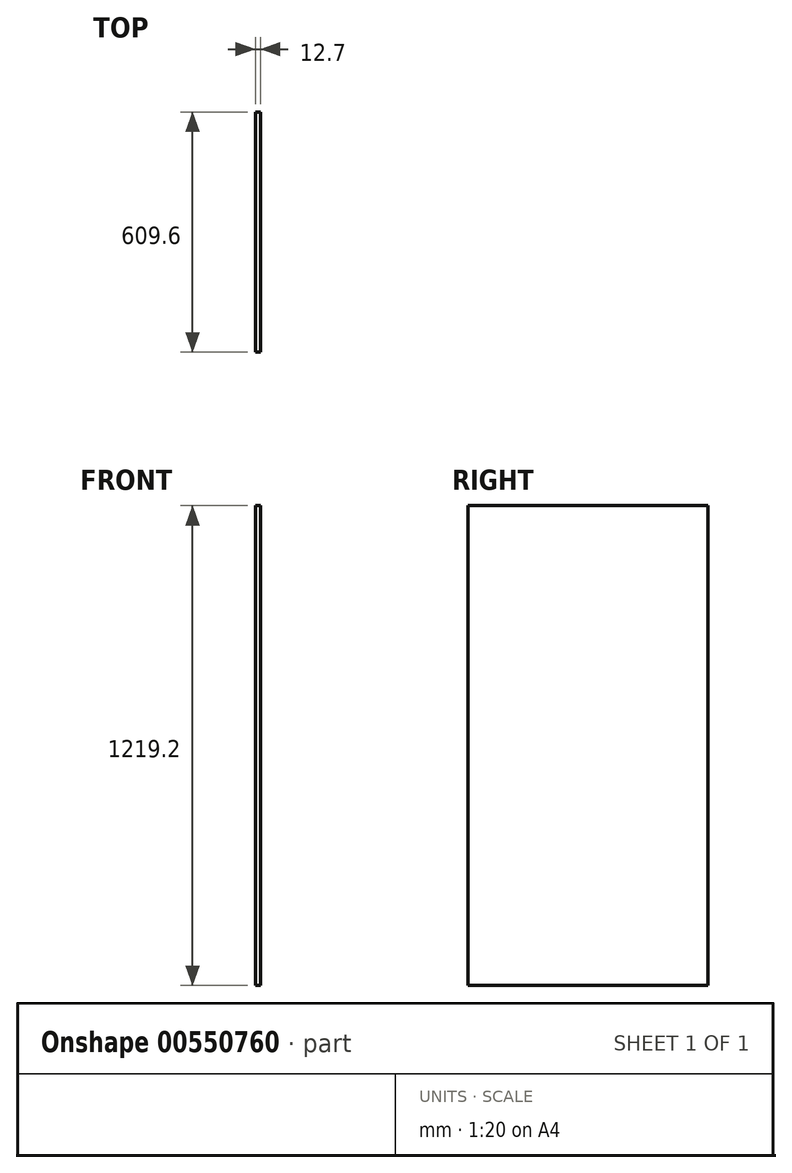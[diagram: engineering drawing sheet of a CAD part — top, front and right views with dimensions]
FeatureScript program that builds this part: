
annotation { "Feature Type Name" : "Feature", "Feature Type Description" : "" }
export const myFeature = defineFeature(function(context is Context, id is Id, definition is map)
    precondition{}
    {
        {
            var Q0;
            Q0=qCreatedBy(makeId("Right.planeOp"),FACE);
            var sketch = newSketch(context, id + "F0", { "sketchPlane" : qUnion([Q0])});
            skLineSegment(sketch, "E0.bottom", {"start": v(0, 0) * mm, "end": v(609.6, 0) * mm});
            skLineSegment(sketch, "E0.top", {"start": v(0, 1219.2) * mm, "end": v(609.6, 1219.2) * mm});
            skLineSegment(sketch, "E0.left", {"start": v(0, 0) * mm, "end": v(0, 1219.2) * mm});
            skLineSegment(sketch, "E0.right", {"start": v(609.6, 0) * mm, "end": v(609.6, 1219.2) * mm});
            skSolve(sketch);
        }
        {
            var Q0;
            Q0 = qSketchRegion(id + "F0", true);
            extrude(context, id + "F1", {"entities" : qUnion([Q0]), "depth" : 12.7 * mm, "offsetDistance" : 25.4 * mm});
        }
    });
